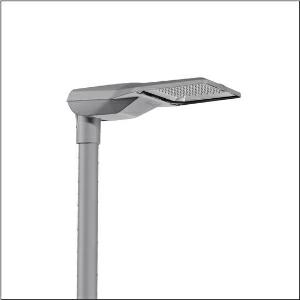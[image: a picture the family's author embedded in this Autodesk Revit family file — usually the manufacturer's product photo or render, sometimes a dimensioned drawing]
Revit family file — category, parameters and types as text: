
# Revit family: streetlight_sl_21_iq_midi___pl52_5xe3h31g08mb_961f
name_source: partatom
category: Lighting Fixtures
units: mm (PartAtom-declared; Revit-internal decimal feet)

## family parameters
Cut with Voids When Loaded = No
Host = Face
Light Source = No
Part Type = Normal
Room Calculation Point = No
Round Connector Dimension = Use Diameter
Shared = No

## types (1)
- --- (1 x LED, 19170 lm, 146.7 W, 3000K)
    Apparent Load = 147 VA
    CIE Flux Codes = 27 59 98 100 100
    Color Rendering = 70
    Color Temperature = 3000K
    Default Elevation = 1800 mm
    Description = Streetlight SL 21 iQ midi, mast luminaire, primary light control with lens, of PMMA, primary optical cover: cover, of toughened safety glass, transparent, light distribution: PL52, light emission: direct distribution, primary light characteristic: asymmetric, installation type: post-top, side-entry, LED, High Power LED, rated luminous flux: 19.170lm, luminous efficacy: 131lm/W, light colour: 730, colour temperature: 3000K, control: Street-Remote, Auto-Match, Temp-Guard, Lumen-Switch, Night-Set, Smart-Wire, Light-Fading, Desk-Remote (wireless, voltage-free reading and setting of iQ features in the workshop via application-optimized NFC function/RFID function), optimised constant luminous flux control (CLO 2.0), presetting dimming linear, mains connection: 230..240V, AC, 50/60Hz, start of lifetime: 147W, end of service life: 161W, reduction: 62W, luminaire housing, of diecast aluminium, powder-coated, Siteco® metallic grey (DB 702S), corrosivity category C5 mid according to DIN EN ISO 12944, please order mast flange separately, inclination adjustable: 0°, 5°, 10°, 15°, sealing non-destructively replaceable, multi-level sealing system, length: 644mm, width: 335mm, height: 110mm, mast flange for spigot size: 42mm (side-entry): 5XC10008XM4, 60/48mm (side-entry/post-top): 5XC10108XM2, 76/60mm (side-entry/post-top): 5XC10108XM1, protection rating (complete): IP66, insulation class (complete): insulation class II (safety insulation), certification: CE, ENEC, ENEC+, VDE, impact resistance: IK09, permissible operating ambient temperature for outdoor applications: -40..+50°C, standard-compliant lighting for roads and squares, packaging unit: 1 piece

Light Distribution: PL52
    Height = 111 mm
    Lamp = 1 x LED
    Lamp Light Flux = 19170 lm
    Lamp Power = 146.7 W
    Lamp count = 1
    Length = 644 mm
    Luminous efficacy = 131 lm/W
    Manufacturer = Siteco
    ModVariant = No
    Model = 5XE3H31G08MB
    Number of Poles = 1
    OnlyDefault = Yes
    Power Factor = 1
    Product Name = Streetlight SL 21 iQ midi | PL52
    Product group = mast luminaire | pylon top
    ProductGroupID = 6100
    Protection Class = Protection class II
    Protection Degree = IP 66
    RLX_Detail_Level = 1
    RLX_Emergency_Light_Flux = 0 lm
    RLX_Emergency_Type = 0
    RLX_Emergency_Type_DB = No
    RlxData = <blob elided: 99973 chars, md5=9cd0c613>
    Socket = socket
    Standby Power = 0 W
    System Light Flux = 19169 lm
    System Power = 147 W
    Type Comments = factory setting: luminous flux: 100 % | dim-lin: 254 | 753 mA
    Type Image = l_1004298.jpg
    URL = http://relux.com
    VarID = @adj_124923
    Voltage = 0 V
    Weight = 0.00 kg
    Width = 336 mm

## geometry (parser evidence)
native form markers: Blend x4, Sweep x10
no freeform markers — native parametric forms only
